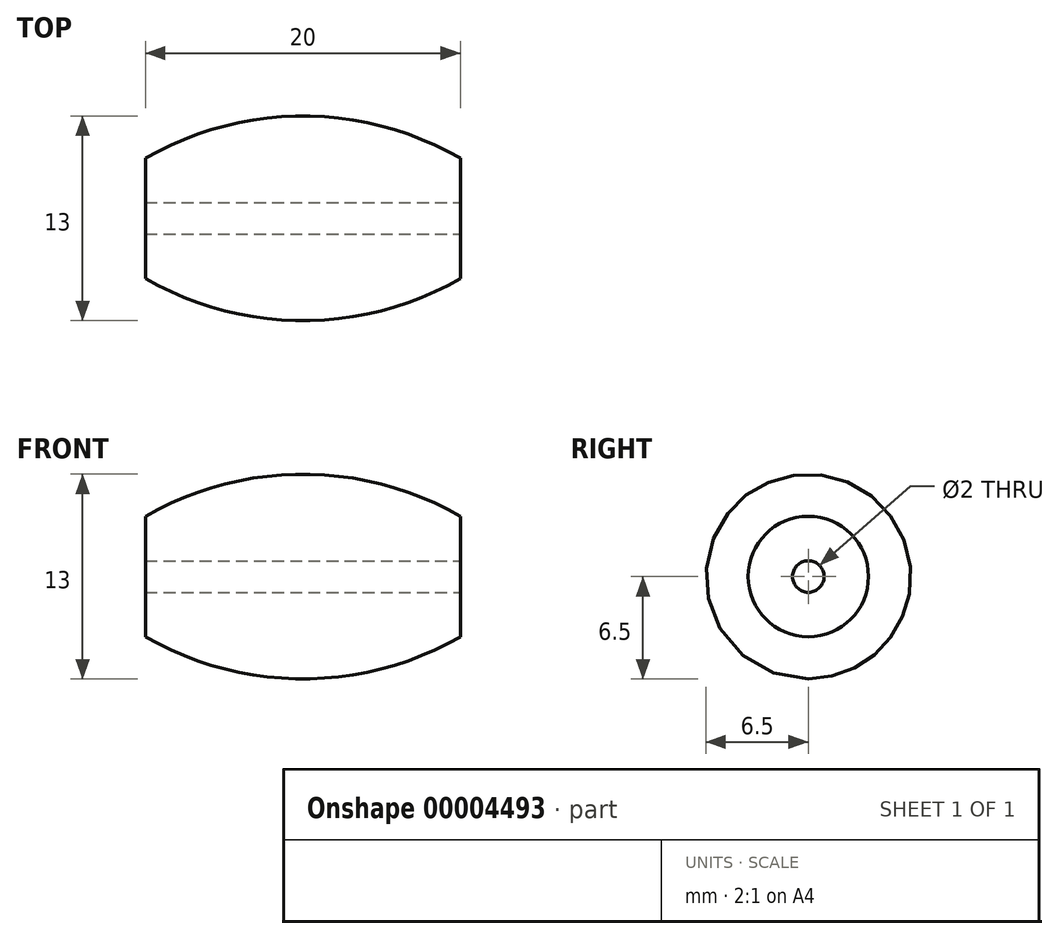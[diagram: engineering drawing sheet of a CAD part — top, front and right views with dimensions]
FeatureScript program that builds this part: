
annotation { "Feature Type Name" : "Feature", "Feature Type Description" : "" }
export const myFeature = defineFeature(function(context is Context, id is Id, definition is map)
    precondition{}
    {
        {
            var Q0;
            Q0=qCreatedBy(makeId("Front.planeOp"),FACE);
            var sketch = newSketch(context, id + "F0", { "sketchPlane" : qUnion([Q0])});
            skLineSegment(sketch, "E0", {"start": v(0, 0) * mm, "end": v(12, 0) * mm, "construction": true});
            skCircle(sketch, "E1", {"center": v(0, 13.5) * mm, "radius": 20 * mm, "construction": true});
            skLineSegment(sketch, "E2", {"start": v(10, -1) * mm, "end": v(10, -3.82) * mm, "construction": true});
            skLineSegment(sketch, "E3", {"start": v(10, -1) * mm, "end": v(12, -1) * mm, "construction": true});
            skLineSegment(sketch, "E4", {"start": v(12, -1) * mm, "end": v(12, 0) * mm, "construction": true});
            skLineSegment(sketch, "E5", {"start": v(0, 0) * mm, "end": v(0, -6.5) * mm, "construction": true});
            skLineSegment(sketch, "E6.0.MirrorCS", {"start": v(-10, -1) * mm, "end": v(-12, -1) * mm, "construction": true});
            skLineSegment(sketch, "E6.1.MirrorCS", {"start": v(-10, -1) * mm, "end": v(-10, -3.82) * mm, "construction": true});
            skLineSegment(sketch, "E6.2.MirrorCS", {"start": v(0, 0) * mm, "end": v(-12, 0) * mm, "construction": true});
            skLineSegment(sketch, "E6.3.MirrorCS", {"start": v(-12, -1) * mm, "end": v(-12, 0) * mm, "construction": true});
            skSolve(sketch);
        }
        {
            var Q0;
            Q0=qCreatedBy(makeId("Front.planeOp"),FACE);
            var sketch = newSketch(context, id + "F1", { "sketchPlane" : qUnion([Q0])});
            skLineSegment(sketch, "E7.0", {"start": v(-10, -1) * mm, "end": v(-10, -3.82) * mm});
            skLineSegment(sketch, "E7.7", {"start": v(10, -1) * mm, "end": v(10, -3.82) * mm});
            skArc(sketch, "E8", {"start": v(-10, -3.82) * mm, "mid": v(0, -6.5) * mm, "end": v(10, -3.82) * mm});
            skLineSegment(sketch, "E9", {"start": v(-10, -1) * mm, "end": v(10, -1) * mm});
            skSolve(sketch);
        }
        {
            var Q0;
            Q0=makeQuery(id+"F1.imprint","IMPRINT",FACE,{"disambiguationData":[TD([[makeQuery(id+"F1.imprint","IMPRINT",EDGE,{"derivedFrom":sQuery(id+"F1.wireOp",EDGE,"E7.0")}),1.0]])]});
            var Q1;
            Q1=sQuery(id+"F0.wireOp",EDGE,"E6.2.MirrorCS");
            revolve(context, id + "F2", {"entities" : qUnion([Q0]), "axis" : qUnion([Q1]), "revolveType" : RevolveType.FULL});
        }
    });
